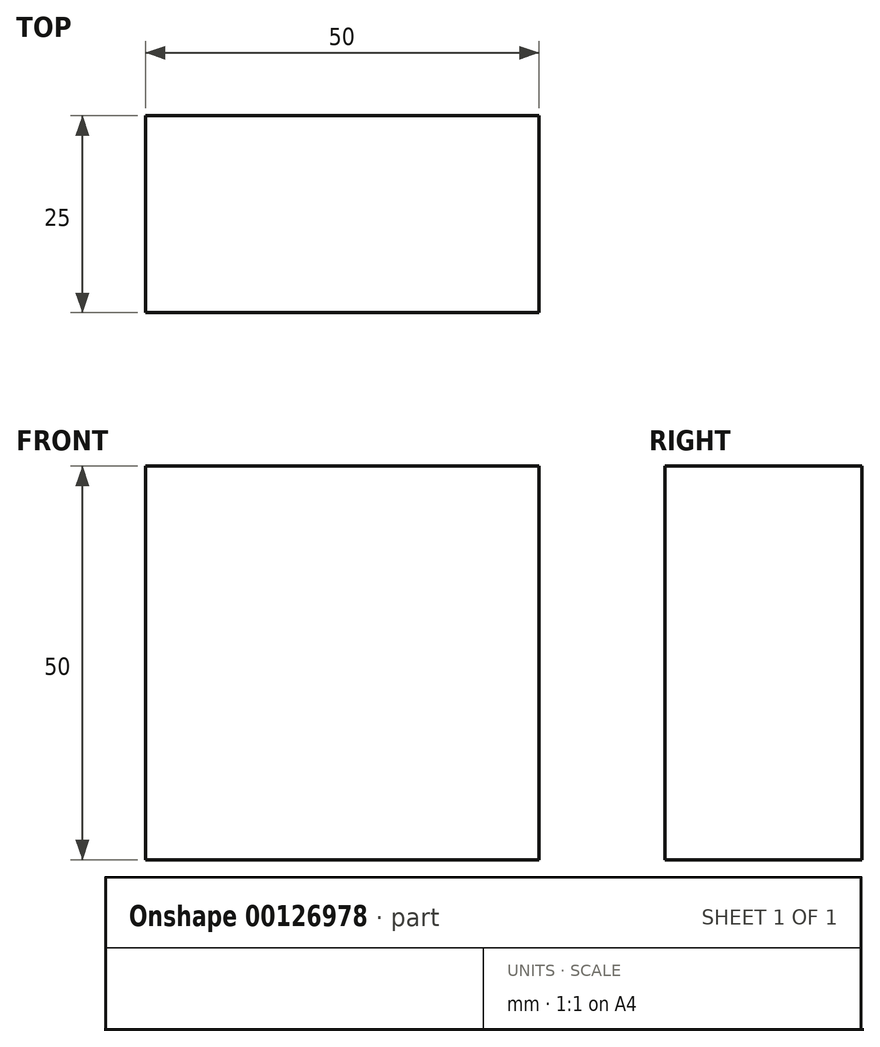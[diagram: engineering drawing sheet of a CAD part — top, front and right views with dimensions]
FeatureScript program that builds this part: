
annotation { "Feature Type Name" : "Feature", "Feature Type Description" : "" }
export const myFeature = defineFeature(function(context is Context, id is Id, definition is map)
    precondition{}
    {
        {
            var Q0;
            Q0=qCreatedBy(makeId("Front.planeOp"),FACE);
            var sketch = newSketch(context, id + "F0", { "sketchPlane" : qUnion([Q0])});
            skLineSegment(sketch, "E0.bottom", {"start": v(0, 0) * mm, "end": v(50, 0) * mm});
            skLineSegment(sketch, "E0.top", {"start": v(0, 50) * mm, "end": v(50, 50) * mm});
            skLineSegment(sketch, "E0.left", {"start": v(0, 0) * mm, "end": v(0, 50) * mm});
            skLineSegment(sketch, "E0.right", {"start": v(50, 0) * mm, "end": v(50, 50) * mm});
            skSolve(sketch);
        }
        {
            var Q0;
            Q0 = qSketchRegion(id + "F0", true);
            extrude(context, id + "F1", {"entities" : qUnion([Q0]), "depth" : 25 * mm});
        }
    });
